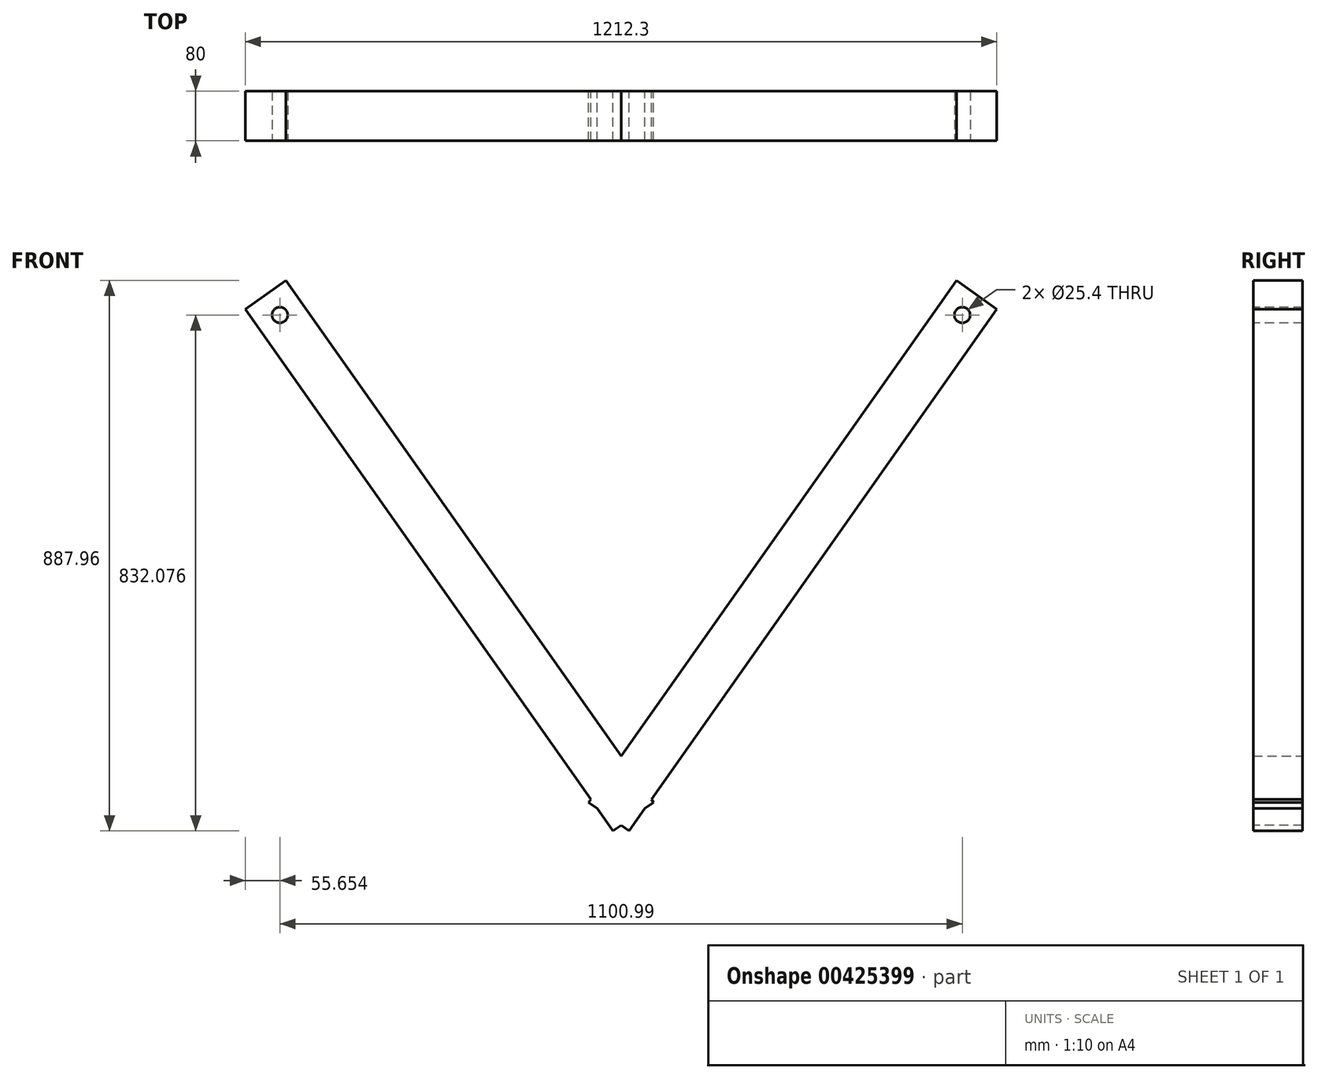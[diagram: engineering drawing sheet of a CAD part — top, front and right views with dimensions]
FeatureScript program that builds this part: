
annotation { "Feature Type Name" : "Feature", "Feature Type Description" : "" }
export const myFeature = defineFeature(function(context is Context, id is Id, definition is map)
    precondition{}
    {
        {
            var Q0;
            Q0=qCreatedBy(makeId("Front.planeOp"),FACE);
            var sketch = newSketch(context, id + "F0", { "sketchPlane" : qUnion([Q0])});
            skLineSegment(sketch, "E0", {"start": v(-52.5, 0) * mm, "end": v(540.94, 841.86) * mm});
            skLineSegment(sketch, "E1", {"start": v(-52.5, 0) * mm, "end": v(12.9, -46.1) * mm});
            skLineSegment(sketch, "E2", {"start": v(12.9, -46.1) * mm, "end": v(606.15, 795.49) * mm});
            skLineSegment(sketch, "E3", {"start": v(606.15, 795.49) * mm, "end": v(540.94, 841.86) * mm});
            skSolve(sketch);
        }
        {
            var Q0;
            Q0 = qSketchRegion(id + "F0", true);
            extrude(context, id + "F1", {"entities" : qUnion([Q0]), "depth" : 80 * mm});
        }
        {
            var Q0;
            Q0=makeQuery(id+"F1.opExtrude","CAP_FACE",FACE,{"disambiguationData":[OSD([sQuery(id+"F0.wireOp",EDGE,"E0"),sQuery(id+"F0.wireOp",EDGE,"E1"),sQuery(id+"F0.wireOp",EDGE,"E2"),sQuery(id+"F0.wireOp",EDGE,"E3")])],"isStart":false});
            var sketch = newSketch(context, id + "F2", { "sketchPlane" : qUnion([Q0])});
            skCircle(sketch, "E4", {"center": v(550.5, 785.98) * mm, "radius": 12.7 * mm});
            skSolve(sketch);
        }
        {
            var Q0;
            Q0 = qSketchRegion(id + "F2", true);
            extrude(context, id + "F3", {"entities" : qUnion([Q0]), "operationType" : NewBodyOperationType.REMOVE, "endBound" : BoundingType.UP_TO_NEXT, "oppositeDirection" : true, "depth" : 25.4 * mm});
        }
        {
            var Q0;
            Q0=makeQuery(id+"F1.opExtrude","SWEPT_BODY",BODY,{"disambiguationData":[OSD([sQuery(id+"F0.wireOp",EDGE,"E0"),sQuery(id+"F0.wireOp",EDGE,"E1"),sQuery(id+"F0.wireOp",EDGE,"E2"),sQuery(id+"F0.wireOp",EDGE,"E3")])]});
            var Q1;
            Q1=qCreatedBy(makeId("Right.planeOp"),FACE);
            mirror(context, id + "F4", {"operationType" : NewBodyOperationType.ADD, "entities" : qUnion([Q0]), "mirrorPlane" : qUnion([Q1])});
        }
    });
